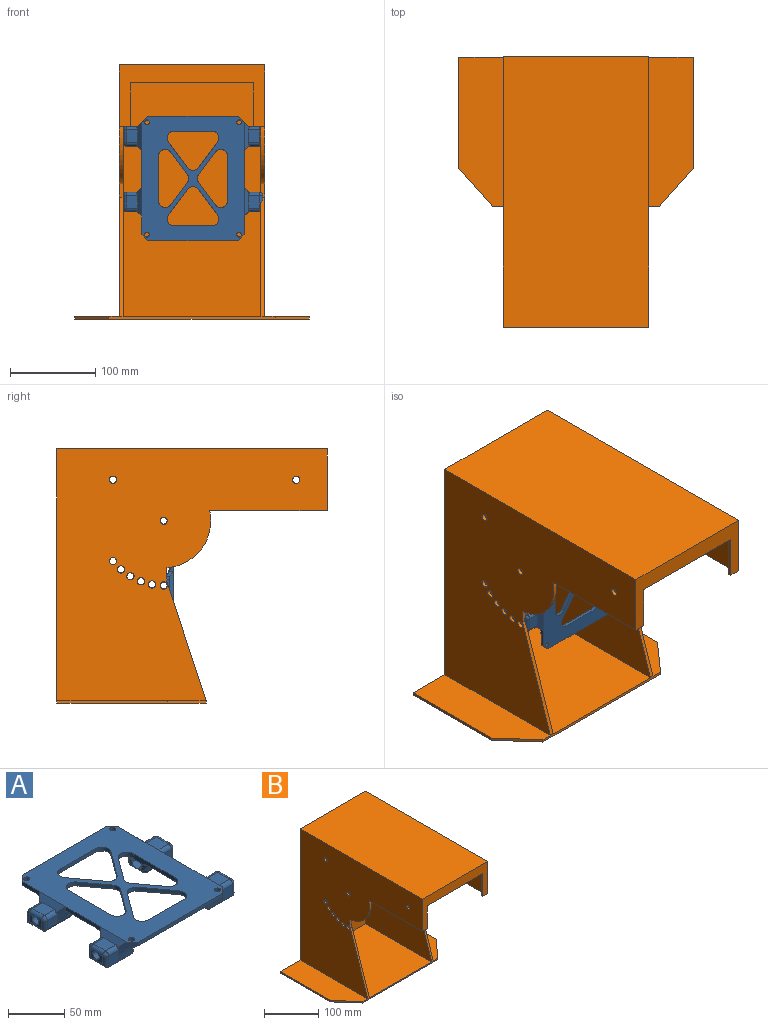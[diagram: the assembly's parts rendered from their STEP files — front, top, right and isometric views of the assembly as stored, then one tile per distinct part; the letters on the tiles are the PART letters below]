
ASSEMBLY  parts=2 mates=5
PART A: 262 faces, bbox 168.6x155.5x27.1 mm
  f0: cylinder r=2.7mm len=5.4mm, axis (0,0,-1), area 84.8mm2, adj f24,f258
  f1: cylinder r=2.7mm len=5.4mm, axis (0,0,-1), area 84.8mm2, adj f24,f261
  f2: bspline ~56.83x16mm, area 37.9mm2, adj f8,f101,f102,f103,f141,f209,f216
  f3: bspline ~58.67x16mm, area 204.4mm2, adj f21,f25,f118,f119,f120,f129,f131,f175
  f4: bspline ~16x16mm, area 0.7mm2, adj f79,f125,f253
  f5: bspline ~16x16mm, area 39.6mm2, adj f79,f127,f150
  f6: cylinder r=4mm len=27mm, axis (1,0,0), area 678.6mm2, adj f43,f107,f228
  f7: cylinder r=4mm len=27mm, axis (1,0,0), area 678.6mm2, adj f28,f100,f213
  f8: plane 52.69x6.38mm, normal (1,0,0), area 241.2mm2, adj f2,f9,f24,f61,f101,f141,f143,f145
  f9: cylinder r=8mm len=14.43mm, axis (0,0,1), area 90.7mm2, adj f8,f24,f59,f101,f106,f138,f139
  f10: cylinder r=8mm len=12.76mm, axis (0,0,1), area 70.9mm2, adj f24,f69,f71,f157,f159,f161,f163,f164
  f11: bspline ~25.8x16mm, area 286.4mm2, adj f14,f20,f108,f109,f110,f159,f189,f231
  f12: bspline ~16x16mm, area 0.7mm2, adj f15,f111,f234
  f13: bspline ~16x16mm, area 39.6mm2, adj f15,f113,f163
  f14: bspline ~16.74x16.74mm, area 10.4mm2, adj f11,f109,f161
  f15: bspline ~56.83x16mm, area 135.2mm2, adj f12,f13,f21,f111,f112,f113,f148,f162
  f16: bspline ~56.83x16mm, area 204.4mm2, adj f21,f25,f104,f105,f106,f134,f136,f138
  f17: plane 22.67x5.56mm, normal (-1,0,0), area 90.4mm2, adj f24,f94,f98,f187,f188
  f18: plane 44.67x5.56mm, normal (-1,0,0), area 180.9mm2, adj f24,f92,f97,f176,f177,f178
  f19: plane 22.67x5.56mm, normal (1,0,0), area 90.4mm2, adj f24,f91,f99,f182,f183
  f20: plane 58x18.67mm, normal (0,0,-1), area 912.3mm2, adj f11,f77,f153,f155,f157,f189
  f21: plane 83.27x58mm, normal (0,0,-1), area 670.7mm2, adj f3,f15,f16,f79,f128,f130,f132,f139
  f22: plane 22x17.5mm, normal (0,0,-1), area 385mm2, adj f80,f85,f166,f180
  f23: plane 22x17.5mm, normal (0,0,-1), area 385mm2, adj f75,f82,f143,f177
  f24: plane 146x120mm, normal (0,0,1), area 10403.9mm2, adj f0,f1,f8,f9,f10,f17,f18,f19
  f25: plane 118x18.67mm, normal (0,0,-1), area 1845.3mm2, adj f3,f16,f40,f41,f81,f83,f133,f135
  f26: plane 29.06x19.06mm, normal (0,0,-1), area 553.2mm2, adj f32,f86,f240,f245,f252,f253,f254
  f27: plane 15x13mm, normal (0,0,1), area 195mm2, adj f87,f241,f246,f249
  f28: plane 15x8mm, normal (-1,0,0), area 73.4mm2, adj f7,f213,f219,f222,f223
  f29: plane 29.06x19.06mm, normal (0,0,-1), area 553.7mm2, adj f44,f230,f234,f237,f238,f239
  f30: plane 15x13mm, normal (0,0,1), area 195mm2, adj f96,f226,f227,f228
  f31: plane 15x8mm, normal (1,0,0), area 73.4mm2, adj f36,f196,f200,f204,f205
  f32: plane 29x12mm, normal (0,-1,0), area 164.1mm2, adj f26,f76,f88,f247,f249,f252
  f33: plane 29.06x15.11mm, normal (0,0,-1), area 439.2mm2, adj f194,f199,f203,f204,f207,f208
  f34: plane 13x8.67mm, normal (0,1,0), area 112.8mm2, adj f91,f197,f205,f207
  f35: cylinder r=4mm len=27mm, axis (1,0,0), area 678.6mm2, adj f45,f121,f246
  f36: cylinder r=4mm len=27mm, axis (1,0,0), area 678.6mm2, adj f31,f114,f196
  f37: plane 106x4mm, normal (0,1,0), area 424mm2, adj f24,f98,f99,f185
  f38: plane 106.01x4.24mm, normal (0,-1,0), area 428.4mm2, adj f24,f88,f95,f189,f190,f191
  f39: plane 44.67x5.56mm, normal (1,0,0), area 180.9mm2, adj f24,f86,f89,f179,f180,f181
  f40: cylinder r=2.7mm len=5.4mm, axis (0,0,-1), area 84.8mm2, adj f24,f25
  f41: cylinder r=2.7mm len=5.4mm, axis (0,0,-1), area 84.8mm2, adj f24,f25
  f42: plane 15x13mm, normal (0,0,1), area 195mm2, adj f90,f192,f196,f197
  f43: plane 15x8mm, normal (-1,0,0), area 73.4mm2, adj f6,f228,f233,f236,f237
  f44: plane 29x12mm, normal (0,-1,0), area 164.1mm2, adj f29,f74,f95,f226,f230,f233
  f45: plane 15x8mm, normal (1,0,0), area 73.4mm2, adj f35,f242,f245,f246,f247
  f46: plane 13x8.67mm, normal (0,1,0), area 112.8mm2, adj f94,f212,f222,f225
  f47: plane 29.06x15.11mm, normal (0,0,-1), area 439.2mm2, adj f215,f216,f220,f223,f224,f225
  f48: plane 15x13mm, normal (0,0,1), area 195mm2, adj f93,f210,f212,f213
  f49: plane 13x8mm, normal (0,1,0), area 104mm2, adj f86,f240,f241,f242
  f50: plane 13x8.67mm, normal (0,-1,0), area 112.8mm2, adj f89,f192,f199,f200
  f51: plane 13x8.67mm, normal (0,1,0), area 112.8mm2, adj f97,f227,f236,f239
  f52: plane 13x8.67mm, normal (0,-1,0), area 112.8mm2, adj f92,f210,f219,f220
  f53: plane 44.29x4mm, normal (0,-1,0), area 177.2mm2, adj f24,f57,f58,f135
  f54: plane 29.87x22.14mm, normal (0.8,0.6,0), area 148.7mm2, adj f24,f56,f57,f132,f134
  f55: plane 29.87x22.14mm, normal (-0.8,0.6,0), area 148.7mm2, adj f24,f56,f58,f128,f129
  f56: cylinder r=8mm len=12.85mm, axis (0,0,1), area 59.7mm2, adj f24,f54,f55,f130
  f57: cylinder r=8mm len=12.76mm, axis (0,0,-1), area 70.7mm2, adj f24,f53,f54,f136,f137
  f58: cylinder r=8mm len=12.76mm, axis (0,0,1), area 70.7mm2, adj f24,f53,f55,f131,f133
  f59: plane 26.21x19.43mm, normal (-0.8,-0.6,0), area 130.5mm2, adj f9,f24,f62,f140
  f60: plane 26.21x19.43mm, normal (-0.8,0.6,0), area 130.5mm2, adj f24,f61,f62,f144
  f61: cylinder r=8mm len=14.43mm, axis (0,0,1), area 85.7mm2, adj f8,f24,f60,f146,f147,f148
  f62: cylinder r=8mm len=9.53mm, axis (0,0,-1), area 40.8mm2, adj f24,f59,f60,f142
  f63: plane 26.21x19.43mm, normal (0.8,-0.6,0), area 130.5mm2, adj f24,f67,f68,f173
  f64: plane 26.21x19.43mm, normal (0.8,0.6,0), area 130.5mm2, adj f24,f66,f67,f171
  f65: plane 52.69x6.38mm, normal (-1,0,0), area 241.2mm2, adj f24,f66,f68,f84,f115,f165,f166,f167
  f66: cylinder r=8mm len=14.43mm, axis (0,0,1), area 85.7mm2, adj f24,f64,f65,f168,f169,f170
  f67: cylinder r=8mm len=9.53mm, axis (0,0,-1), area 40.8mm2, adj f24,f63,f64,f172
  f68: cylinder r=8mm len=14.43mm, axis (0,0,1), area 90.7mm2, adj f24,f63,f65,f115,f120,f174,f175
  f69: plane 44.29x4mm, normal (0,1,0), area 177.2mm2, adj f10,f24,f73,f155
  f70: plane 29.87x22.14mm, normal (-0.8,-0.6,0), area 148.7mm2, adj f24,f72,f73,f154,f156
  f71: plane 29.87x22.14mm, normal (0.8,-0.6,0), area 148.7mm2, adj f10,f24,f72,f160,f162
  f72: cylinder r=8mm len=12.85mm, axis (0,0,1), area 59.7mm2, adj f24,f70,f71,f158
  f73: cylinder r=8mm len=12.76mm, axis (0,0,-1), area 70.9mm2, adj f24,f69,f70,f149,f150,f151,f152,f153
  f74: bspline ~36.52x15.49mm, area 232.2mm2, adj f44,f95,f189,f231,f256,f257
  f75: bspline ~36.7x16mm, area 420.7mm2, adj f23,f97,f145,f147,f178,f235,f238,f239
  f76: bspline ~36.52x15.49mm, area 242.4mm2, adj f32,f88,f190,f191,f251,f259,f260
  f77: bspline ~25.8x16mm, area 286.8mm2, adj f20,f78,f122,f123,f124,f151,f190,f251
  f78: bspline ~16.74x16.74mm, area 10.4mm2, adj f77,f123,f149
  f79: bspline ~56.83x16mm, area 135.2mm2, adj f4,f5,f21,f125,f126,f127,f152,f154
  f80: bspline ~36.68x16mm, area 420.7mm2, adj f22,f86,f167,f168,f181,f250,f254
  f81: bspline ~37.79x16mm, area 475.9mm2, adj f25,f94,f188,f217,f224,f225
  f82: bspline ~36.66x16mm, area 416.8mm2, adj f23,f92,f141,f176,f209,f215,f220
  f83: bspline ~36.73x16mm, area 475.9mm2, adj f25,f91,f182,f202,f207,f208
  f84: bspline ~56.83x16mm, area 37.9mm2, adj f65,f115,f116,f117,f165,f193,f203
  f85: bspline ~36.69x16mm, area 416.8mm2, adj f22,f89,f165,f179,f193,f194,f199
  f86: plane 22.68x11.68mm, normal (0.71,0.71,0), area 44mm2, adj f26,f39,f49,f80,f87,f181,f240,f241
  f87: plane 33.56x6.73mm, normal (0.71,0,0.71), area 202.8mm2, adj f24,f27,f86,f88,f241,f249
  f88: plane 21.05x13.73mm, normal (0.71,-0.71,0), area 104.9mm2, adj f24,f32,f38,f76,f87,f191,f249,f260
  f89: plane 22.3x11.8mm, normal (0.71,-0.71,0), area 43.7mm2, adj f39,f50,f85,f90,f179,f192,f199
  f90: plane 33.56x6.73mm, normal (0.71,0,0.71), area 202.8mm2, adj f24,f42,f89,f91,f192,f197
  f91: plane 22.25x11.74mm, normal (0.71,0.71,0), area 43.7mm2, adj f19,f34,f83,f90,f182,f197,f207
  f92: plane 22.25x11.74mm, normal (-0.71,-0.71,0), area 43.7mm2, adj f18,f52,f82,f93,f176,f210,f220
  f93: plane 33.56x6.73mm, normal (-0.71,0,0.71), area 202.8mm2, adj f24,f48,f92,f94,f210,f212
  f94: plane 22.3x11.8mm, normal (-0.71,0.71,0), area 43.7mm2, adj f17,f46,f81,f93,f188,f212,f225
  f95: plane 21.05x13.73mm, normal (-0.71,-0.71,0), area 104.3mm2, adj f24,f38,f44,f74,f96,f189,f226,f257
  f96: plane 33.56x6.73mm, normal (-0.71,0,0.71), area 202.8mm2, adj f24,f30,f95,f97,f226,f227
  f97: plane 18.24x7.73mm, normal (-0.71,0.71,0), area 43.7mm2, adj f18,f51,f75,f96,f178,f227,f239
  f98: plane 7x7mm, normal (-0.71,0.71,0), area 39.6mm2, adj f17,f24,f37,f186
  f99: plane 7x7mm, normal (0.71,0.71,0), area 39.6mm2, adj f19,f24,f37,f184
  f100: plane 15.01x13mm, normal (1,0,0), area 96.1mm2, adj f7,f101,f102,f103,f104,f105,f106
  f101: plane 14.54x6.5mm, normal (0,0.5,-0.87), area 101.5mm2, adj f2,f8,f9,f100,f102,f106
  f102: plane 11.72x7.51mm, normal (0,1,0), area 79.6mm2, adj f2,f100,f101,f103
  f103: plane 10.36x6.75mm, normal (0,0.5,0.87), area 74.2mm2, adj f2,f100,f102,f104,f216
  f104: plane 10.36x6.75mm, normal (0,-0.5,0.87), area 74.2mm2, adj f16,f100,f103,f105,f216
  f105: plane 11.72x7.51mm, normal (0,-1,0), area 79.6mm2, adj f16,f100,f104,f106
  f106: plane 15.27x6.97mm, normal (0,-0.5,-0.87), area 102mm2, adj f9,f16,f100,f101,f105,f138
  f107: plane 15.01x13mm, normal (1,0,0), area 96.1mm2, adj f6,f108,f109,f110,f111,f112,f113
  f108: plane 11.72x7.51mm, normal (0,1,0), area 79.6mm2, adj f11,f107,f109,f110
  f109: plane 25.1x7.02mm, normal (0,0.5,-0.87), area 120mm2, adj f11,f14,f107,f108,f113,f161
  f110: plane 10.36x6.75mm, normal (0,0.5,0.87), area 74.2mm2, adj f11,f107,f108,f111,f234
  f111: plane 10.36x6.75mm, normal (0,-0.5,0.87), area 74.1mm2, adj f12,f15,f107,f110,f112,f234
  f112: plane 11.72x7.51mm, normal (0,-1,0), area 79.6mm2, adj f15,f107,f111,f113
  f113: plane 24.61x6.52mm, normal (0,-0.5,-0.87), area 124.7mm2, adj f13,f15,f107,f109,f112,f161,f163
  f114: plane 15.01x13mm, normal (-1,0,0), area 96.1mm2, adj f36,f115,f116,f117,f118,f119,f120
  f115: plane 14.54x6.5mm, normal (0,0.5,-0.87), area 101.5mm2, adj f65,f68,f84,f114,f116,f120
  f116: plane 11.72x7.51mm, normal (0,1,0), area 79.6mm2, adj f84,f114,f115,f117
  f117: plane 10.36x6.75mm, normal (0,0.5,0.87), area 74.2mm2, adj f84,f114,f116,f118,f203
  f118: plane 10.36x6.75mm, normal (0,-0.5,0.87), area 74.2mm2, adj f3,f114,f117,f119,f203
  f119: plane 11.72x7.51mm, normal (0,-1,0), area 79.6mm2, adj f3,f114,f118,f120
  f120: plane 15.27x6.97mm, normal (0,-0.5,-0.87), area 102mm2, adj f3,f68,f114,f115,f119,f175
  f121: plane 15.01x13mm, normal (-1,0,0), area 96.1mm2, adj f35,f122,f123,f124,f125,f126,f127
  f122: plane 11.72x7.51mm, normal (0,1,0), area 79.6mm2, adj f77,f121,f123,f124
  f123: plane 25.1x7.02mm, normal (0,0.5,-0.87), area 120mm2, adj f77,f78,f121,f122,f127,f149
  f124: plane 10.36x6.75mm, normal (0,0.5,0.87), area 74.2mm2, adj f77,f121,f122,f125,f253
  f125: plane 10.36x6.75mm, normal (0,-0.5,0.87), area 74.2mm2, adj f4,f79,f121,f124,f126,f253
  f126: plane 11.72x7.51mm, normal (0,-1,0), area 79.6mm2, adj f79,f121,f125,f127
  f127: plane 24.61x6.52mm, normal (0,-0.5,-0.87), area 124.7mm2, adj f5,f79,f121,f123,f126,f149,f150
  f128: plane 29.96x22.57mm, normal (-0.57,0.42,-0.71), area 51.7mm2, adj f21,f55,f129,f130
  f129: bspline ~1.18x1.1mm, area 0.9mm2, adj f3,f55,f128,f131
  f130: cone r=9mm half-angle=45deg, axis (0,0,-1), area 22.4mm2, adj f21,f56,f128,f132
  f131: bspline ~11.19x2.95mm, area 16.1mm2, adj f3,f58,f129,f133
  f132: plane 29.96x22.57mm, normal (0.57,0.42,-0.71), area 51.7mm2, adj f21,f54,f130,f134
  f133: cone r=9mm half-angle=45deg, axis (0,0,-1), area 10.4mm2, adj f25,f58,f131,f135
  f134: bspline ~1.18x1.1mm, area 0.9mm2, adj f16,f54,f132,f136
  f135: plane 44.29x1mm, normal (0,-0.71,-0.71), area 62.6mm2, adj f25,f53,f133,f137
  f136: bspline ~11.19x2.95mm, area 16.1mm2, adj f16,f57,f134,f137
  f137: cone r=9mm half-angle=45deg, axis (0,0,-1), area 10.4mm2, adj f25,f57,f135,f136
  f138: bspline ~11.93x7.54mm, area 18.6mm2, adj f9,f16,f106,f139
  f139: cone r=9mm half-angle=45deg, axis (0,0,-1), area 6.4mm2, adj f9,f21,f138,f140
  f140: plane 26.8x20.23mm, normal (-0.57,-0.42,-0.71), area 46.1mm2, adj f21,f59,f139,f142
  f141: bspline ~14.16x3.28mm, area 18.6mm2, adj f2,f8,f82,f143,f209
  f142: cone r=9mm half-angle=45deg, axis (0,0,-1), area 15.3mm2, adj f21,f62,f140,f144
  f143: plane 22x1mm, normal (0.71,0,-0.71), area 31.1mm2, adj f8,f23,f141,f145
  f144: plane 26.8x20.23mm, normal (-0.57,0.42,-0.71), area 46.1mm2, adj f21,f60,f142,f146
  f145: bspline ~4.21x1.07mm, area 5.9mm2, adj f8,f75,f143,f147
  f146: cone r=9mm half-angle=45deg, axis (0,0,-1), area 6.4mm2, adj f21,f61,f144,f148
  f147: bspline ~6.15x3.36mm, area 8.6mm2, adj f61,f75,f145,f148,f235
  f148: bspline ~10.09x3.76mm, area 14.6mm2, adj f15,f61,f146,f147,f235
  f149: bspline ~2.84x1.7mm, area 3.2mm2, adj f73,f78,f123,f127,f150,f151
  f150: bspline ~5.66x1.81mm, area 7.1mm2, adj f5,f73,f127,f149,f152
  f151: bspline ~2.17x1.9mm, area 2.7mm2, adj f73,f77,f149,f153
  f152: bspline ~1.69x1.57mm, area 1.9mm2, adj f73,f79,f150,f154
  f153: cone r=9mm half-angle=45deg, axis (0,0,-1), area 10.4mm2, adj f20,f73,f151,f155
  f154: bspline ~1.18x1.1mm, area 0.9mm2, adj f70,f79,f152,f156
  f155: plane 44.29x1mm, normal (0,0.71,-0.71), area 62.6mm2, adj f20,f69,f153,f157
  f156: plane 29.96x22.57mm, normal (-0.57,-0.42,-0.71), area 51.7mm2, adj f21,f70,f154,f158
  f157: cone r=9mm half-angle=45deg, axis (0,0,-1), area 10.4mm2, adj f10,f20,f155,f159
  f158: cone r=9mm half-angle=45deg, axis (0,0,-1), area 22.4mm2, adj f21,f72,f156,f160
  f159: bspline ~7.97x2.91mm, area 2.7mm2, adj f10,f11,f157,f161
  f160: plane 29.96x22.57mm, normal (0.57,-0.42,-0.71), area 51.7mm2, adj f21,f71,f158,f162
  f161: bspline ~2.83x1.7mm, area 3.2mm2, adj f10,f14,f109,f113,f159,f163
  f162: bspline ~1.18x1.1mm, area 0.9mm2, adj f15,f71,f160,f164
  f163: bspline ~5.66x1.81mm, area 7.2mm2, adj f10,f13,f113,f161,f164
  f164: bspline ~1.69x1.57mm, area 1.9mm2, adj f10,f15,f162,f163
  f165: bspline ~14.16x3.28mm, area 18.6mm2, adj f65,f84,f85,f166,f193
  f166: plane 22x1mm, normal (-0.71,0,-0.71), area 31.1mm2, adj f22,f65,f165,f167
  f167: bspline ~4.21x1.07mm, area 5.9mm2, adj f65,f80,f166,f168
  f168: bspline ~5.93x3.13mm, area 8.6mm2, adj f66,f80,f167,f169,f250
  f169: bspline ~10.44x4.39mm, area 14.6mm2, adj f66,f79,f168,f170,f250
  f170: cone r=9mm half-angle=45deg, axis (0,0,-1), area 6.4mm2, adj f21,f66,f169,f171
  f171: plane 26.8x20.23mm, normal (0.57,0.42,-0.71), area 46.1mm2, adj f21,f64,f170,f172
  f172: cone r=9mm half-angle=45deg, axis (0,0,-1), area 15.3mm2, adj f21,f67,f171,f173
  f173: plane 26.8x20.23mm, normal (0.57,-0.42,-0.71), area 46.1mm2, adj f21,f63,f172,f174
  f174: cone r=9mm half-angle=45deg, axis (0,0,-1), area 6.4mm2, adj f21,f68,f173,f175
  f175: bspline ~11.93x7.54mm, area 18.6mm2, adj f3,f68,f120,f174
  f176: bspline ~11.84x2.1mm, area 14.9mm2, adj f18,f82,f92,f177
  f177: plane 22x1mm, normal (-0.71,0,-0.71), area 31.1mm2, adj f18,f23,f176,f178
  f178: bspline ~11x1.85mm, area 14.9mm2, adj f18,f75,f97,f177
  f179: bspline ~11.84x2.1mm, area 14.9mm2, adj f39,f85,f89,f180
  f180: plane 22x1mm, normal (0.71,0,-0.71), area 31.1mm2, adj f22,f39,f179,f181
  f181: bspline ~11.84x2.1mm, area 14.9mm2, adj f39,f80,f86,f180
  f182: bspline ~11.84x2.1mm, area 14.9mm2, adj f19,f83,f91,f183
  f183: plane 11x1mm, normal (0.71,0,-0.71), area 15.3mm2, adj f19,f25,f182,f184
  f184: plane 7.41x7.41mm, normal (0.5,0.5,-0.71), area 13.4mm2, adj f25,f99,f183,f185
  f185: plane 106x1mm, normal (0,0.71,-0.71), area 149.3mm2, adj f25,f37,f184,f186
  f186: plane 7.41x7.41mm, normal (-0.5,0.5,-0.71), area 13.4mm2, adj f25,f98,f185,f187
  f187: plane 11x1mm, normal (-0.71,0,-0.71), area 15.3mm2, adj f17,f25,f186,f188
  f188: bspline ~11.84x2.1mm, area 14.9mm2, adj f17,f81,f94,f187
  f189: plane 84.35x2.35mm, normal (0,-0.71,-0.71), area 126.4mm2, adj f11,f20,f38,f74,f95,f190,f231
  f190: bspline ~11.91x2.12mm, area 11.1mm2, adj f38,f76,f77,f189,f191,f251
  f191: plane 17.9x1.1mm, normal (0,-0.79,-0.61), area 19.9mm2, adj f38,f76,f88,f190
  f192: cylinder r=4mm len=13mm, axis (-1,0,0), area 78mm2, adj f42,f50,f89,f90,f195
  f193: bspline ~12.71x9.07mm, area 74.4mm2, adj f84,f85,f165,f198
  f194: cylinder r=4mm len=11.06mm, axis (-1,0,0), area 68mm2, adj f33,f85,f198,f199
  f195: sphere r=4mm, area 25.1mm2, adj f192,f196,f200
  f196: cylinder r=4mm len=15mm, axis (0,1,0), area 90.6mm2, adj f31,f36,f42,f195,f201
  f197: cylinder r=4mm len=13mm, axis (-1,0,0), area 78mm2, adj f34,f42,f90,f91,f201
  f198: sphere r=4mm, area 33.1mm2, adj f193,f194,f203
  f199: cylinder r=4mm len=20.8mm, axis (-1,0,0), area 111.5mm2, adj f33,f50,f85,f89,f194,f200,f204
  f200: cylinder r=4mm len=10.86mm, axis (0,0,-1), area 60.3mm2, adj f31,f50,f195,f199,f204
  f201: sphere r=4mm, area 16mm2, adj f196,f197,f205
  f202: bspline ~19.99x19.99mm, area 62.8mm2, adj f3,f83,f206
  f203: cylinder r=4mm len=15.11mm, axis (0,-1,0), area 82.4mm2, adj f3,f33,f84,f117,f118,f198,f206
  f204: cylinder r=4mm len=20.71mm, axis (0,-1,0), area 112.4mm2, adj f31,f33,f199,f200,f205,f207
  f205: cylinder r=4mm len=10.86mm, axis (0,0,1), area 60.3mm2, adj f31,f34,f201,f204,f207
  f206: sphere r=4mm, area 15.5mm2, adj f202,f203,f208
  f207: cylinder r=4mm len=20.8mm, axis (-1,0,0), area 111.5mm2, adj f33,f34,f83,f91,f204,f205,f208
  f208: cylinder r=4mm len=11.06mm, axis (-1,0,0), area 68mm2, adj f33,f83,f206,f207
  f209: bspline ~12.71x9.07mm, area 74.4mm2, adj f2,f82,f141,f211
  f210: cylinder r=4mm len=13mm, axis (-1,0,0), area 78mm2, adj f48,f52,f92,f93,f214
  f211: sphere r=4mm, area 24.3mm2, adj f209,f215,f216
  f212: cylinder r=4mm len=13mm, axis (-1,0,0), area 78mm2, adj f46,f48,f93,f94,f218
  f213: cylinder r=4mm len=15mm, axis (0,-1,0), area 90.6mm2, adj f7,f28,f48,f214,f218
  f214: sphere r=4mm, area 25.1mm2, adj f210,f213,f219
  f215: cylinder r=4mm len=11.06mm, axis (-1,0,0), area 68mm2, adj f47,f82,f211,f220
  f216: cylinder r=4mm len=15.11mm, axis (0,1,0), area 82.4mm2, adj f2,f16,f47,f103,f104,f211,f221
  f217: bspline ~19.99x19.99mm, area 62.8mm2, adj f16,f81,f221
  f218: sphere r=4mm, area 34.3mm2, adj f212,f213,f222
  f219: cylinder r=4mm len=10.86mm, axis (0,0,1), area 60.3mm2, adj f28,f52,f214,f220,f223
  f220: cylinder r=4mm len=20.8mm, axis (-1,0,0), area 111.5mm2, adj f47,f52,f82,f92,f215,f219,f223
  f221: sphere r=4mm, area 15.5mm2, adj f216,f217,f224
  f222: cylinder r=4mm len=10.86mm, axis (0,0,-1), area 60.3mm2, adj f28,f46,f218,f223,f225
  f223: cylinder r=4mm len=20.71mm, axis (0,1,0), area 112.4mm2, adj f28,f47,f219,f220,f222,f225
  f224: cylinder r=4mm len=11.06mm, axis (-1,0,0), area 68mm2, adj f47,f81,f221,f225
  f225: cylinder r=4mm len=20.8mm, axis (-1,0,0), area 111.5mm2, adj f46,f47,f81,f94,f222,f223,f224
  f226: cylinder r=4mm len=13mm, axis (1,0,0), area 78mm2, adj f30,f44,f95,f96,f229
  f227: cylinder r=4mm len=13mm, axis (1,0,0), area 78mm2, adj f30,f51,f96,f97,f232
  f228: cylinder r=4mm len=15mm, axis (0,-1,0), area 90.6mm2, adj f6,f30,f43,f229,f232
  f229: sphere r=4mm, area 25.1mm2, adj f226,f228,f233
  f230: bspline ~4x4mm, area 0.7mm2, adj f29,f44,f231,f234
  f231: bspline ~16.32x16.15mm, area 99mm2, adj f11,f74,f189,f230,f234
  f232: sphere r=4mm, area 34.3mm2, adj f227,f228,f236
  f233: cylinder r=4mm len=12mm, axis (0,0,1), area 62.8mm2, adj f43,f44,f229,f237
  f234: cylinder r=4mm len=21.83mm, axis (0,1,0), area 105.4mm2, adj f11,f12,f15,f29,f110,f111,f230,f231
  f235: bspline ~15.07x11.88mm, area 87.4mm2, adj f15,f75,f147,f148,f234,f238
  f236: cylinder r=4mm len=10.86mm, axis (0,0,-1), area 60.3mm2, adj f43,f51,f232,f237,f239
  f237: cylinder r=4mm len=21.86mm, axis (0,1,0), area 115.9mm2, adj f29,f43,f233,f236,f239
  f238: cylinder r=4mm len=13.83mm, axis (1,0,0), area 76.6mm2, adj f29,f75,f234,f235,f239
  f239: cylinder r=4mm len=20.8mm, axis (1,0,0), area 111.5mm2, adj f29,f51,f75,f97,f236,f237,f238
  f240: cylinder r=4mm len=13mm, axis (-1,0,0), area 69.1mm2, adj f26,f49,f86,f243
  f241: cylinder r=4mm len=13mm, axis (1,0,0), area 78mm2, adj f27,f49,f86,f87,f244
  f242: cylinder r=4mm len=8mm, axis (0,0,1), area 50.3mm2, adj f45,f49,f243,f244
  f243: sphere r=4mm, area 16mm2, adj f240,f242,f245
  f244: sphere r=4mm, area 16mm2, adj f241,f242,f246
  f245: cylinder r=4mm len=19mm, axis (0,-1,0), area 106.8mm2, adj f26,f45,f243,f247
  f246: cylinder r=4mm len=15mm, axis (0,1,0), area 90.6mm2, adj f27,f35,f45,f244,f248
  f247: cylinder r=4mm len=12mm, axis (0,0,-1), area 62.8mm2, adj f32,f45,f245,f248
  f248: sphere r=4mm, area 16mm2, adj f246,f247,f249
  f249: cylinder r=4mm len=13mm, axis (1,0,0), area 78mm2, adj f27,f32,f87,f88,f248
  f250: bspline ~13.46x11.87mm, area 79mm2, adj f79,f80,f168,f169,f255
  f251: bspline ~16.76x16.19mm, area 100.8mm2, adj f76,f77,f190,f252,f253
  f252: bspline ~4.05x4.02mm, area 0.7mm2, adj f26,f32,f251,f253
  f253: cylinder r=4mm len=19.06mm, axis (0,-1,0), area 96.9mm2, adj f4,f26,f77,f79,f124,f125,f251,f252
  f254: cylinder r=4mm len=20mm, axis (1,0,0), area 110.8mm2, adj f26,f80,f86,f255
  f255: sphere r=4mm, area 15.5mm2, adj f250,f253,f254
  f256: plane 2.64x0.18mm, normal (0,0,1), area 0.3mm2, adj f74,f257
  f257: cylinder r=5mm len=10mm, axis (0,0,-1), area 101.4mm2, adj f74,f95,f256,f258
  f258: plane 10x10mm, normal (0,0,-1), area 52.9mm2, adj f0,f95,f257
  f259: plane 2.64x0.18mm, normal (0,0,1), area 0.3mm2, adj f76,f260
  f260: cylinder r=5mm len=10mm, axis (0,0,-1), area 101.4mm2, adj f76,f88,f259,f261
  f261: plane 10x10mm, normal (0,0,-1), area 52.9mm2, adj f1,f88,f260
PART B: 48 faces, bbox 275x317x298.2 mm
  f0: plane 137.76x13mm, normal (0,0,-1), area 633.7mm2, adj f15,f16,f19,f21,f24,f27
  f1: plane 137.76x13mm, normal (0,0,-1), area 633.7mm2, adj f2,f15,f20,f21,f23,f28
  f2: cylinder r=55.25mm len=66.87mm, axis (-1,0,0), area 417.4mm2, adj f1,f3,f20,f23
  f3: plane 15.63x4.4mm, normal (0,-1,0), area 68.8mm2, adj f2,f4,f20,f23
  f4: plane 140x46mm, normal (0,-0.95,0.31), area 648.4mm2, adj f3,f10,f20,f23
  f5: plane 175x52.3mm, normal (0,0,1), area 8252.5mm2, adj f7,f8,f9,f10,f20
  f6: plane 130x3.2mm, normal (1,0,0), area 416mm2, adj f7,f11,f12,f13
  f7: plane 298.2x275mm, normal (0,1,0), area 51148mm2, adj f5,f6,f8,f12,f13,f14,f19,f20
  f8: plane 130x3.2mm, normal (-1,0,0), area 416mm2, adj f5,f7,f9,f13
  f9: plane 45x40mm, normal (-0.75,-0.66,0), area 192.7mm2, adj f5,f8,f10,f13
  f10: plane 195x3.2mm, normal (0,-1,0), area 624mm2, adj f4,f5,f9,f11,f12,f13,f18,f22
  f11: plane 45x40mm, normal (0.75,-0.66,0), area 192.7mm2, adj f6,f10,f12,f13
  f12: plane 175x52.3mm, normal (0,0,1), area 8252.5mm2, adj f6,f7,f10,f11,f19
  f13: plane 275x175mm, normal (0,0,-1), area 46325mm2, adj f6,f7,f8,f9,f10,f11
  f14: plane 317x170.4mm, normal (0,0,1), area 54016.8mm2, adj f7,f15,f19,f20
  f15: plane 170.4x72.5mm, normal (0,-1,0), area 4917.4mm2, adj f0,f1,f14,f19,f20,f27,f28,f29
  f16: cylinder r=55.25mm len=66.87mm, axis (-1,0,0), area 417.4mm2, adj f0,f17,f19,f24
  f17: plane 15.63x4.4mm, normal (0,-1,0), area 68.8mm2, adj f16,f18,f19,f24
  f18: plane 140x46mm, normal (0,-0.95,0.31), area 648.4mm2, adj f10,f17,f19,f24
  f19: plane 317x295mm, normal (1,0,0), area 57184.9mm2, adj f0,f7,f12,f14,f15,f16,f17,f18
  f20: plane 317x295mm, normal (-1,0,0), area 57184.9mm2, adj f1,f2,f3,f4,f5,f7,f14,f15
  f21: plane 161.6x69.3mm, normal (0,1,0), area 3762.3mm2, adj f0,f1,f23,f24,f26,f27,f28,f29
  f22: plane 171.8x161.6mm, normal (0,0,1), area 27762.9mm2, adj f10,f23,f24,f25
  f23: plane 310.6x291.8mm, normal (1,0,0), area 55015mm2, adj f1,f2,f3,f4,f21,f22,f25,f26
  f24: plane 310.6x291.8mm, normal (-1,0,0), area 55015mm2, adj f0,f16,f17,f18,f21,f22,f25,f26
  f25: plane 291.8x161.6mm, normal (0,-1,0), area 47154.9mm2, adj f22,f23,f24,f26
  f26: plane 310.6x161.6mm, normal (0,0,-1), area 50193mm2, adj f21,f23,f24,f25
  f27: plane 51.5x3.2mm, normal (-1,0,0), area 164.8mm2, adj f0,f15,f21,f29
  f28: plane 51.5x3.2mm, normal (1,0,0), area 164.8mm2, adj f1,f15,f21,f29
  f29: plane 144.4x3.2mm, normal (0,0,-1), area 462.1mm2, adj f15,f21,f27,f28
  f30: cylinder r=4.25mm len=8.5mm, axis (-1,0,0), area 117.5mm2, adj f19,f24
  f31: cylinder r=4.25mm len=8.5mm, axis (-1,0,0), area 117.5mm2, adj f19,f24
  f32: cylinder r=4.25mm len=8.5mm, axis (-1,0,0), area 117.5mm2, adj f19,f24
  f33: cylinder r=4.25mm len=8.5mm, axis (-1,0,0), area 117.5mm2, adj f19,f24
  f34: cylinder r=4.25mm len=8.5mm, axis (-1,0,0), area 117.5mm2, adj f19,f24
  f35: cylinder r=4.25mm len=8.5mm, axis (-1,0,0), area 117.5mm2, adj f19,f24
  f36: cylinder r=4.25mm len=8.5mm, axis (-1,0,0), area 117.5mm2, adj f19,f24
  f37: cylinder r=4.25mm len=8.5mm, axis (-1,0,0), area 117.5mm2, adj f19,f24
  f38: cylinder r=4.25mm len=8.5mm, axis (-1,0,0), area 117.5mm2, adj f19,f24
  f39: cylinder r=4.25mm len=8.5mm, axis (-1,0,0), area 117.5mm2, adj f20,f23
  f40: cylinder r=4.25mm len=8.5mm, axis (-1,0,0), area 117.5mm2, adj f20,f23
  f41: cylinder r=4.25mm len=8.5mm, axis (-1,0,0), area 117.5mm2, adj f20,f23
  f42: cylinder r=4.25mm len=8.5mm, axis (-1,0,0), area 117.5mm2, adj f20,f23
  f43: cylinder r=4.25mm len=8.5mm, axis (-1,0,0), area 117.5mm2, adj f20,f23
  f44: cylinder r=4.25mm len=8.5mm, axis (-1,0,0), area 117.5mm2, adj f20,f23
  f45: cylinder r=4.25mm len=8.5mm, axis (-1,0,0), area 117.5mm2, adj f20,f23
  f46: cylinder r=4.25mm len=8.5mm, axis (-1,0,0), area 117.5mm2, adj f20,f23
  f47: cylinder r=4.25mm len=8.5mm, axis (-1,0,0), area 117.5mm2, adj f20,f23
PLACE A rot(axis=(0,-0.71,0.71),180deg) t=(61.2,-47.57,237.95)mm
PLACE B t=(0,-2.82,0)mm
MATE cylindrical A.f7 <-> B.f35  axis (-1,0,0) through (-67.3,-40.57,137.95)mm
MATE cylindrical A.f6 <-> B.f2  axis (-1,0,0) through (-67.3,-40.57,213.95)mm
MATE cylindrical A.f7 <-> B.f31  axis (-1,0,0) through (-67.3,-40.57,137.95)mm
MATE planar B.f23 <-> A.f45  axis (1,0,0) through (-80.8,-26.03,171.33)mm
MATE cylindrical A.f7 <-> B.f30  axis (-1,0,0) through (-67.3,-40.57,137.95)mm
